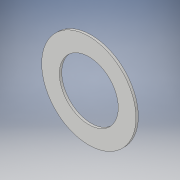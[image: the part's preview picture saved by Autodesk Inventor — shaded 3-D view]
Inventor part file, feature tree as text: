
AUTODESK INVENTOR PART (.ipt)
format: ipt  version: 2019 (Build 230136000, 136)  size: 98,816 bytes
history: native  units: mm
features: extrude x1, sketch x1
ambient origin geometry x8: Origin, YZ Plane, XZ Plane, XY Plane, X Axis, Y Axis, Z Axis, Center Point
bodies: Solid1 (feature_tree)
feature tree (2):
  extrude  "Extrusion1"  Depth=2.0mm
  sketch  "Sketch1"  dims[d0=50.0mm d1=15.0mm d2=2.0mm d3=0.0mm]
